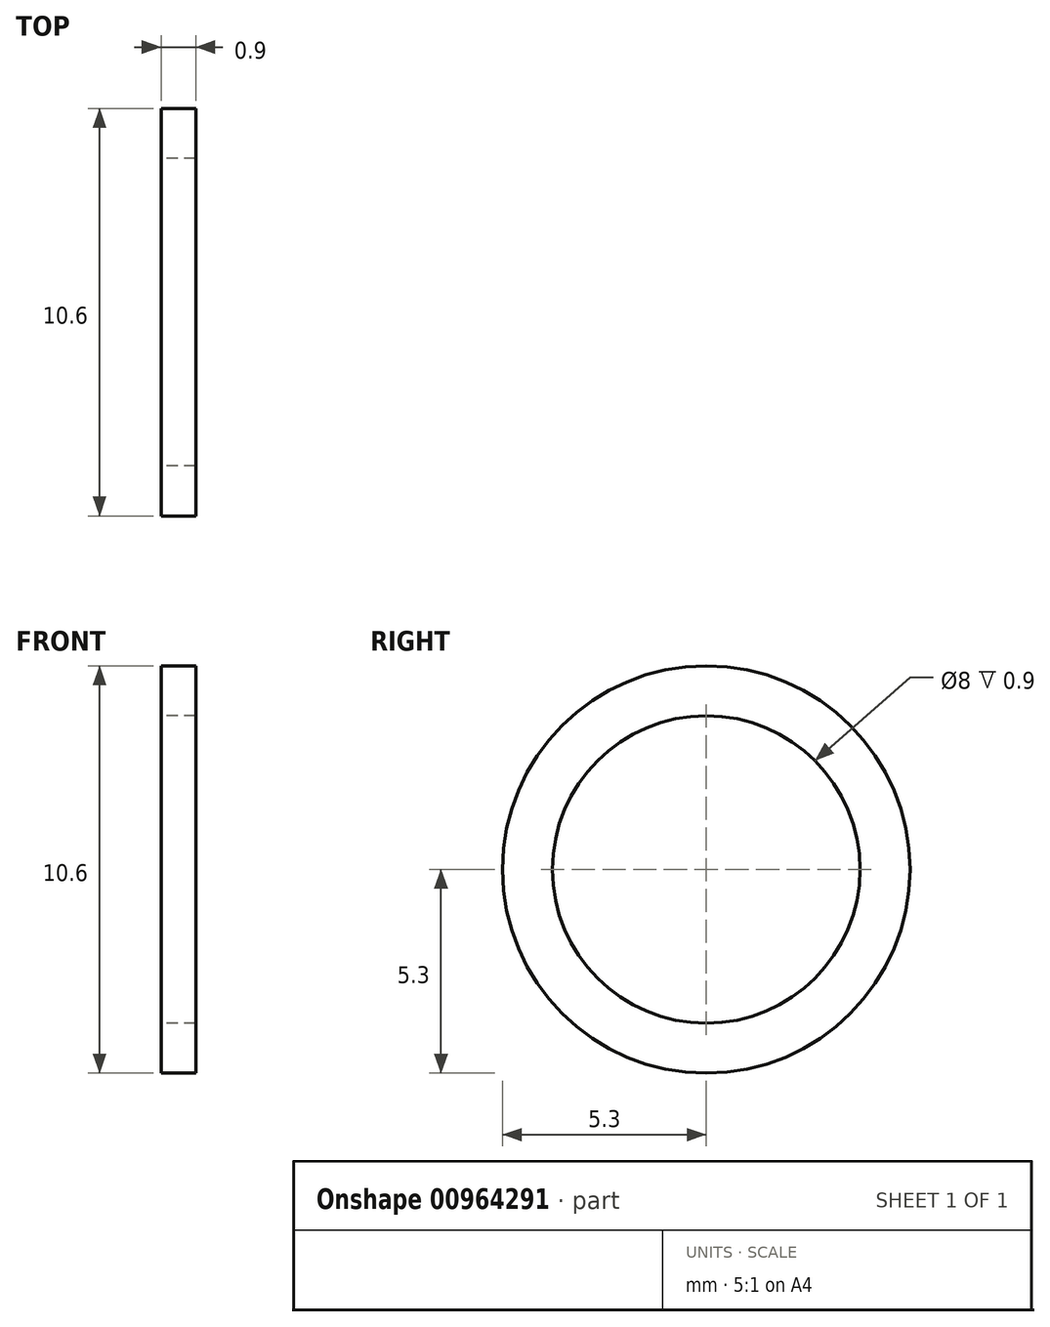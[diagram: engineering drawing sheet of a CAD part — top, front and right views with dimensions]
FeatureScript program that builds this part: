
annotation { "Feature Type Name" : "Feature", "Feature Type Description" : "" }
export const myFeature = defineFeature(function(context is Context, id is Id, definition is map)
    precondition{}
    {
        {
            var Q0;
            Q0=qCreatedBy(makeId("Right.planeOp"),FACE);
            var sketch = newSketch(context, id + "F0", { "sketchPlane" : qUnion([Q0])});
            skCircle(sketch, "E0", {"center": v(0, 0) * mm, "radius": 5.3 * mm});
            skCircle(sketch, "E1", {"center": v(0, 0) * mm, "radius": 4 * mm});
            skSolve(sketch);
        }
        {
            var Q0;
            Q0 = qSketchRegion(id + "F0", true);
            extrude(context, id + "F1", {"entities" : qUnion([Q0]), "depth" : .9 * mm, "offsetDistance" : 25 * mm, "symmetric" : true});
        }
    });
